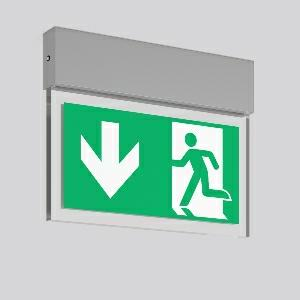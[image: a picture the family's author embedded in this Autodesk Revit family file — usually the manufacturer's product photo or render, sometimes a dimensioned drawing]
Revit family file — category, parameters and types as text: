
# Revit family: halyxx_671744_004_1_04_e8ef
name_source: partatom
category: Lighting Fixtures
units: mm (PartAtom-declared; Revit-internal decimal feet)

## family parameters
Cut with Voids When Loaded = No
Host = Face
Light Source = No
Part Type = Normal
Room Calculation Point = No
Round Connector Dimension = Use Diameter
Shared = No

## types (1)
- HALYXX (1 x LED Modul 840, 95 lm, 4000)
    Apparent Load = 4 VA
    Approval mark = CE
    CIE Flux Codes = 18 45 74 52 100
    Color Rendering = 80
    Color Temperature = 4000
    Default Elevation = 1800 mm
    Description = Series: HALYXX
Luminaire for escape route identification. Housing: extruded aluminium profile, anodised or powder-coated. Display panel: highly transparent panel, plastic, with legend on one side/both sides. Electronic ballast included. Self-contained system with automatic self-test and feedback to the RZB monitoring system MULTIDIGIT. Please indicate legend number when placing your order! 
Colour: anodised aluminium
Length: 340 mm
Width: 40 mm
Height: 270 mm
Weight: 2.18 kg
Operating mode: maintained power mode
Viewing Distance: 30 m
Duration time: 3 h
Lamp: LED
Socket: without socket
Colour temperature: 4000K
Colour rendering index (CRI): 80
System power: 4.2 W
Rated luminous flux: 95 lm
Luminous flux, emergency: 25
System power, emergency: -
Control gear: Electronic transformer
Protection class: I
Type of protection: IP 40
    Height = 270 mm
    Lamp = 1 x LED Modul 840
    Lamp Light Flux = 95 lm
    Lamp count = 1
    Length = 340 mm
    Lifetime = 50000 h
    Luminous efficacy = 23 lm/W
    Manufacturer = RZB
    ModVariant = No
    Model = 671744.004.1.04
    Mounting Place = Ceiling
    Mounting Type = Surface mounted
    Number of Poles = 1
    OnlyDefault = Yes
    Power Factor = 1
    Product Name = HALYXX
    Product group = Surface mounted ceiling luminaires
    ProductGroupID = 303
    Protection Class = Protection class I
    Protection Degree = IP 40
    RLX_Detail_Level = 1
    RLX_Emergency_Light_Flux = 25 lm
    RLX_Emergency_Type = 3
    RLX_Emergency_Type_DB = Yes
    RlxData = <blob elided: 55077 chars, md5=d06f7116>
    Socket = socket
    Standby Power = 0 W
    System Light Flux = 95 lm
    System Power = 4 W
    Type Comments = Product without accessories
    Type Image = 671744.004.jpg
    URL = http://relux.com
    VarID = ---
    Voltage = 230 V
    Voltage Range = 220-240 V
    Weight = 0.00 kg
    Width = 40 mm  [stored 0.131234 ft]

note: [stored X ft] marks values corroborated as IEEE doubles in the binary element streams (Revit-internal decimal feet)

## geometry (parser evidence)
native form markers: Blend x4, Sweep x13
no freeform markers — native parametric forms only
